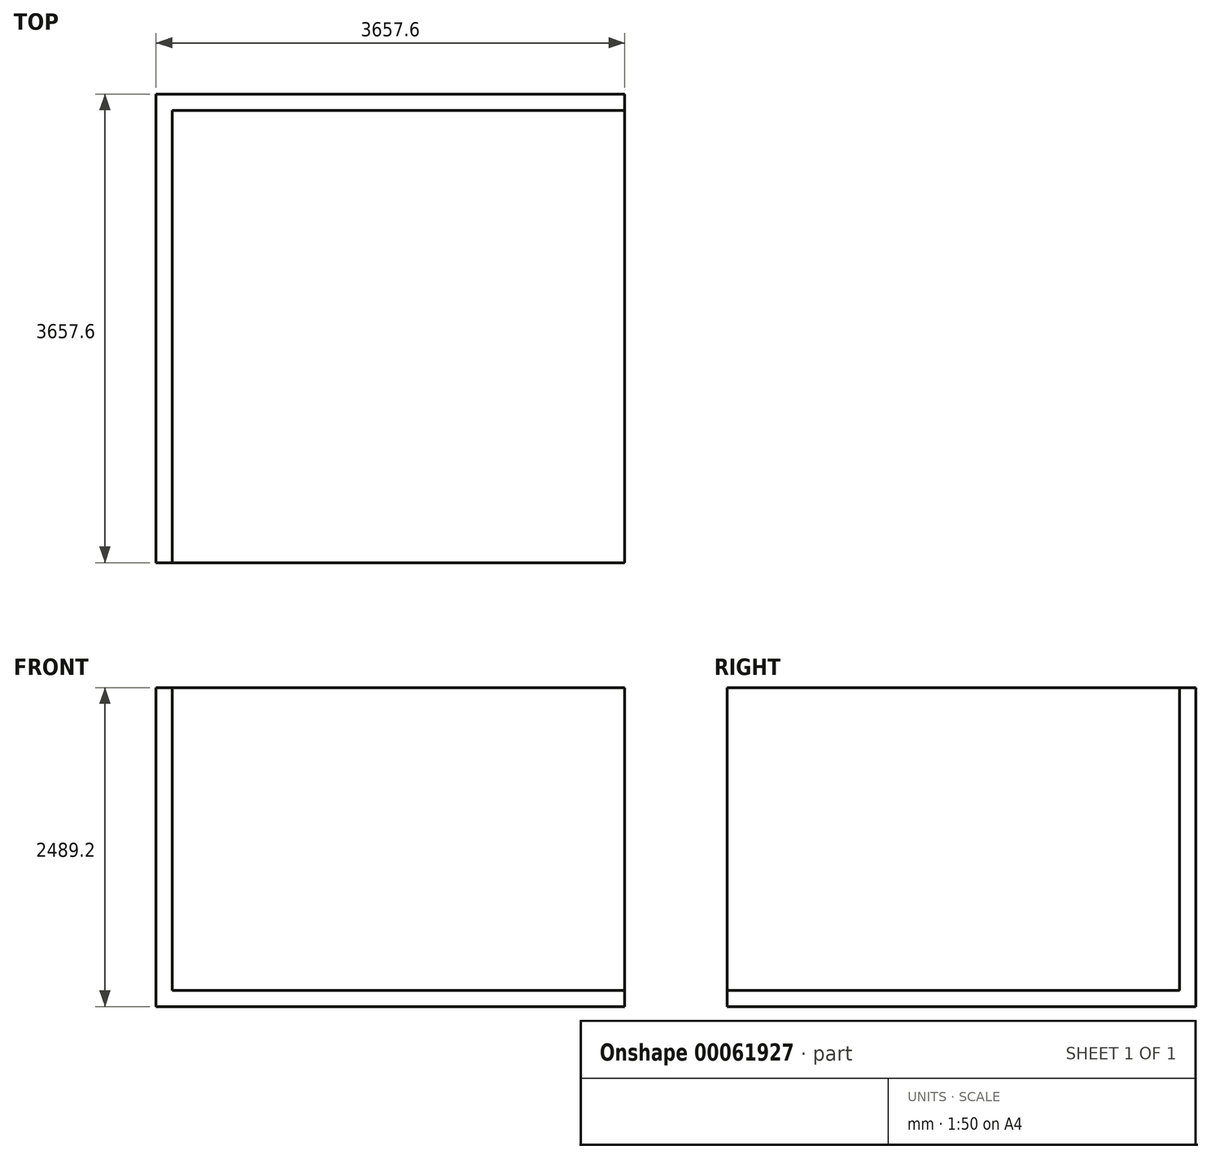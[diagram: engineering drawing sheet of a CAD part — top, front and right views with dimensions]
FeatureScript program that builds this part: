
annotation { "Feature Type Name" : "Feature", "Feature Type Description" : "" }
export const myFeature = defineFeature(function(context is Context, id is Id, definition is map)
    precondition{}
    {
        {
            var Q0;
            Q0=qCreatedBy(makeId("Top.planeOp"),FACE);
            var sketch = newSketch(context, id + "F0", { "sketchPlane" : qUnion([Q0])});
            skLineSegment(sketch, "E0.bottom", {"start": v(0, 0) * mm, "end": v(3657.6, 0) * mm});
            skLineSegment(sketch, "E0.top", {"start": v(0, -3657.6) * mm, "end": v(3657.6, -3657.6) * mm});
            skLineSegment(sketch, "E0.left", {"start": v(0, 0) * mm, "end": v(0, -3657.6) * mm});
            skLineSegment(sketch, "E0.right", {"start": v(3657.6, 0) * mm, "end": v(3657.6, -3657.6) * mm});
            skSolve(sketch);
        }
        {
            var Q0;
            Q0 = qSketchRegion(id + "F0", true);
            extrude(context, id + "F1", {"entities" : qUnion([Q0]), "depth" : 2489.2 * mm});
        }
        {
            var Q0;
            Q0=makeQuery(id+"F1.opExtrude","CAP_FACE",FACE,{"disambiguationData":[OSD([sQuery(id+"F0.wireOp",EDGE,"E0.bottom"),sQuery(id+"F0.wireOp",EDGE,"E0.top"),sQuery(id+"F0.wireOp",EDGE,"E0.left"),sQuery(id+"F0.wireOp",EDGE,"E0.right")])],"isStart":false});
            var Q1;
            Q1=makeQuery(id+"F1.opExtrude","SWEPT_FACE",FACE,{"disambiguationData":[OSD([sQuery(id+"F0.wireOp",EDGE,"E0.top")])]});
            var Q2;
            Q2=makeQuery(id+"F1.opExtrude","SWEPT_FACE",FACE,{"disambiguationData":[OSD([sQuery(id+"F0.wireOp",EDGE,"E0.right")])]});
            shell(context, id + "F2", {"entities" : qUnion([Q0, Q1, Q2]), "thickness" : 127 * mm});
        }
    });
